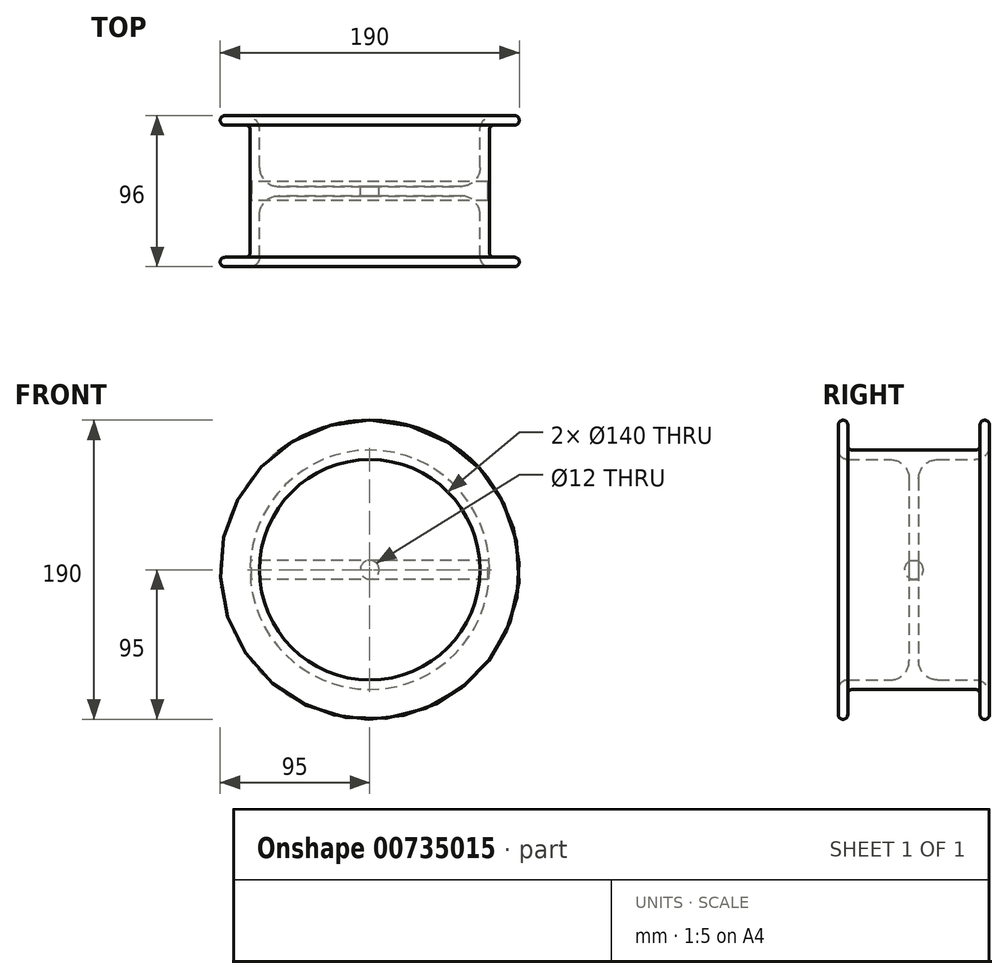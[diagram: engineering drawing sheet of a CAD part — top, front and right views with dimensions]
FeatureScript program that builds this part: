
annotation { "Feature Type Name" : "Feature", "Feature Type Description" : "" }
export const myFeature = defineFeature(function(context is Context, id is Id, definition is map)
    precondition{}
    {
        {
            var Q0;
            Q0=qCreatedBy(makeId("Right.planeOp"),FACE);
            var sketch = newSketch(context, id + "F0", { "sketchPlane" : qUnion([Q0])});
            skLineSegment(sketch, "E0", {"start": v(0, 0) * mm, "end": v(-30, 0) * mm, "construction": true});
            skLineSegment(sketch, "E1.MirrorCS", {"start": v(0, 0) * mm, "end": v(21.42, 0) * mm, "construction": true});
            skLineSegment(sketch, "E2.0", {"start": v(0, 6) * mm, "end": v(3, 6) * mm});
            skLineSegment(sketch, "E3.0", {"start": v(0, 6) * mm, "end": v(-3, 6) * mm});
            skLineSegment(sketch, "E4.0", {"start": v(-3, 6) * mm, "end": v(-3, 58) * mm});
            skLineSegment(sketch, "E5.0", {"start": v(3, 6) * mm, "end": v(3, 58) * mm});
            skLineSegment(sketch, "E6", {"start": v(-15, 70) * mm, "end": v(-42, 70) * mm});
            skLineSegment(sketch, "E7", {"start": v(15, 70) * mm, "end": v(39, 70) * mm});
            skLineSegment(sketch, "E8", {"start": v(48, 79) * mm, "end": v(48, 92) * mm});
            skLineSegment(sketch, "E9", {"start": v(45, 95) * mm, "end": v(45, 95) * mm});
            skLineSegment(sketch, "E10", {"start": v(42, 92) * mm, "end": v(42, 79) * mm});
            skLineSegment(sketch, "E11", {"start": v(39, 76) * mm, "end": v(-39, 76) * mm});
            skLineSegment(sketch, "E12", {"start": v(-42, 79) * mm, "end": v(-42, 92) * mm});
            skLineSegment(sketch, "E13", {"start": v(-45, 95) * mm, "end": v(-45, 95) * mm});
            skLineSegment(sketch, "E14", {"start": v(-48, 92) * mm, "end": v(-48, 76) * mm});
            skLineSegment(sketch, "E15", {"start": v(0, 6) * mm, "end": v(0, 300) * mm, "construction": true});
            skPoint(sketch, "E16.visualSharp", {"position": v(-48, 95) * mm});
            skArc(sketch, "E16.filletArc", {"start": v(-45, 95) * mm, "mid": v(-47.12, 94.12) * mm, "end": v(-48, 92) * mm});
            skPoint(sketch, "E17.visualSharp", {"position": v(-42, 95) * mm});
            skArc(sketch, "E17.filletArc", {"start": v(-42, 92) * mm, "mid": v(-42.88, 94.12) * mm, "end": v(-45, 95) * mm});
            skPoint(sketch, "E18.visualSharp", {"position": v(-48, 70) * mm});
            skArc(sketch, "E18.filletArc", {"start": v(-48, 76) * mm, "mid": v(-46.24, 71.76) * mm, "end": v(-42, 70) * mm});
            skArc(sketch, "E19.filletArc", {"start": v(-42, 79) * mm, "mid": v(-41.12, 76.88) * mm, "end": v(-39, 76) * mm});
            skPoint(sketch, "E20.visualSharp", {"position": v(42, 76) * mm});
            skArc(sketch, "E20.filletArc", {"start": v(39, 76) * mm, "mid": v(41.12, 76.88) * mm, "end": v(42, 79) * mm});
            skPoint(sketch, "E21.visualSharp", {"position": v(48, 70) * mm});
            skArc(sketch, "E21.filletArc", {"start": v(39, 70) * mm, "mid": v(45.36, 72.64) * mm, "end": v(48, 79) * mm});
            skPoint(sketch, "E22.visualSharp", {"position": v(42, 95) * mm});
            skArc(sketch, "E22.filletArc", {"start": v(45, 95) * mm, "mid": v(42.88, 94.12) * mm, "end": v(42, 92) * mm});
            skPoint(sketch, "E23.visualSharp", {"position": v(48, 95) * mm});
            skArc(sketch, "E23.filletArc", {"start": v(48, 92) * mm, "mid": v(47.12, 94.12) * mm, "end": v(45, 95) * mm});
            skPoint(sketch, "E24.visualSharp", {"position": v(-3, 70) * mm});
            skArc(sketch, "E24.filletArc", {"start": v(-3, 58) * mm, "mid": v(-6.51, 66.49) * mm, "end": v(-15, 70) * mm});
            skPoint(sketch, "E25.visualSharp", {"position": v(3, 70) * mm});
            skArc(sketch, "E25.filletArc", {"start": v(15, 70) * mm, "mid": v(6.51, 66.49) * mm, "end": v(3, 58) * mm});
            skSolve(sketch);
        }
        {
            var Q0;
            Q0=makeQuery(id+"F0.imprint","IMPRINT",FACE,{"disambiguationData":[TD([[makeQuery(id+"F0.imprint","IMPRINT",EDGE,{"derivedFrom":sQuery(id+"F0.wireOp",EDGE,"E2.0")}),1.0]])]});
            var Q1;
            Q1=sQuery(id+"F0.wireOp",EDGE,"E0");
            revolve(context, id + "F1", {"surfaceOperationType" : NewSurfaceOperationType.NEW, "entities" : qUnion([Q0]), "axis" : qUnion([Q1]), "revolveType" : RevolveType.FULL});
        }
        {
            var Q0;
            Q0=qCreatedBy(makeId("Right.planeOp"),FACE);
            var sketch = newSketch(context, id + "F2", { "sketchPlane" : qUnion([Q0])});
            skCircle(sketch, "E26", {"center": v(0, 0) * mm, "radius": 6 * mm});
            skCircle(sketch, "E27", {"center": v(21.59, 0) * mm, "radius": 5.9 * mm});
            skSolve(sketch);
        }
        {
            var Q0;
            Q0=makeQuery(id+"F2.imprint","IMPRINT",FACE,{"disambiguationData":[TD([[makeQuery(id+"F2.imprint","IMPRINT",EDGE,{"derivedFrom":sQuery(id+"F2.wireOp",EDGE,"E26")}),1.0]])]});
            extrude(context, id + "F3", {"entities" : qUnion([Q0]), "endBound" : BoundingType.SYMMETRIC, "depth" : 150 * mm, "offsetDistance" : 25 * mm});
        }
    });
